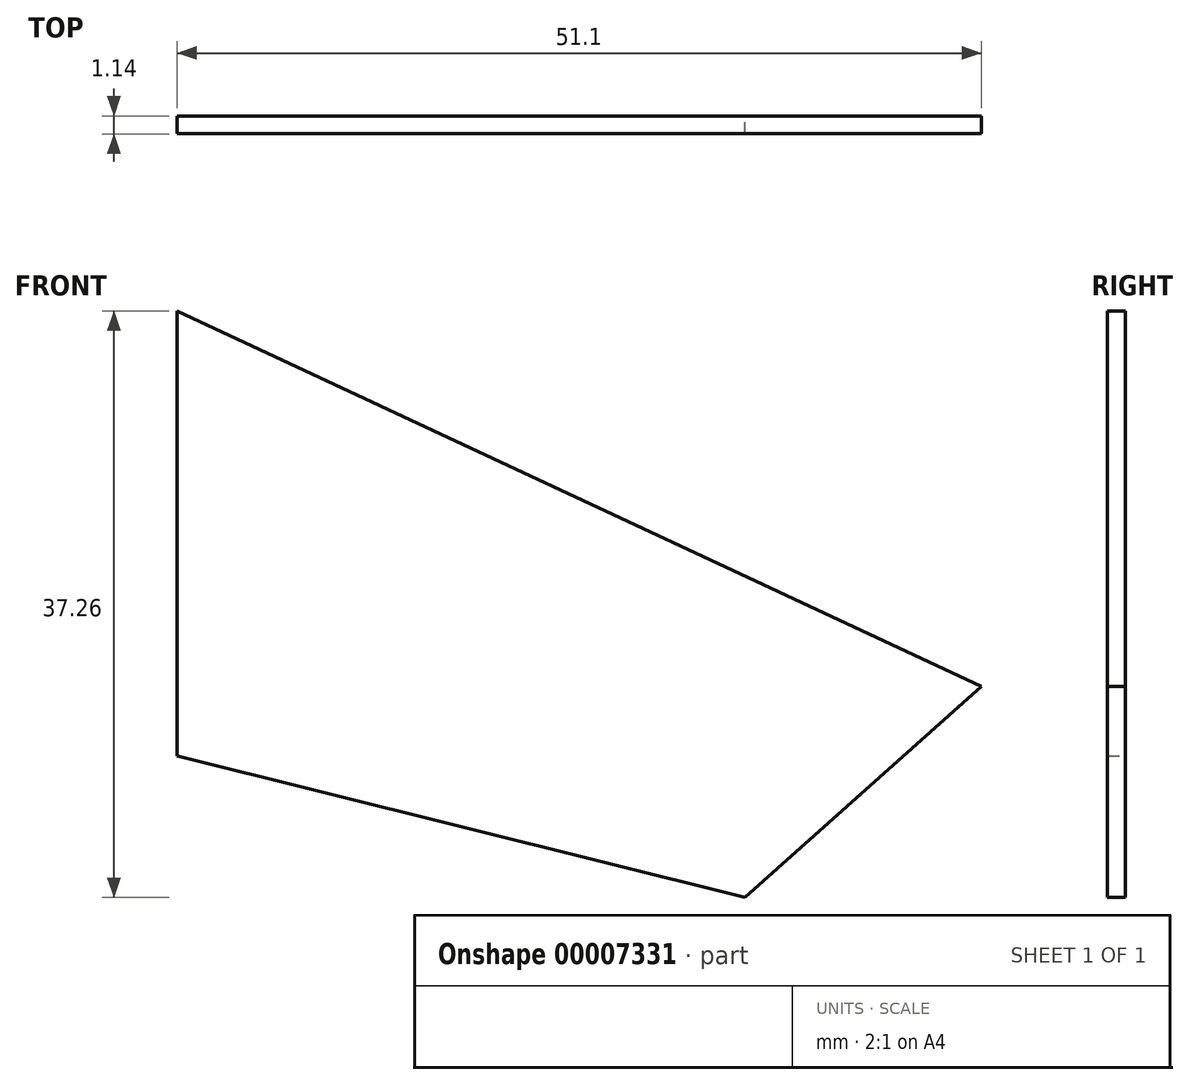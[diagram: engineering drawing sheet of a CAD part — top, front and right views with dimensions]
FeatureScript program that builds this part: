
annotation { "Feature Type Name" : "Feature", "Feature Type Description" : "" }
export const myFeature = defineFeature(function(context is Context, id is Id, definition is map)
    precondition{}
    {
        {
            var Q0;
            Q0=qCreatedBy(makeId("Front.planeOp"),FACE);
            var sketch = newSketch(context, id + "F0", { "sketchPlane" : qUnion([Q0])});
            skLineSegment(sketch, "E0", {"start": v(0, 0) * mm, "end": v(0, 28.27) * mm});
            skLineSegment(sketch, "E1", {"start": v(0, 28.27) * mm, "end": v(51.1, 4.42) * mm});
            skLineSegment(sketch, "E2", {"start": v(51.1, 4.42) * mm, "end": v(36.07, -9) * mm});
            skLineSegment(sketch, "E3", {"start": v(36.07, -9) * mm, "end": v(0, 0) * mm});
            skSolve(sketch);
        }
        {
            var Q0;
            Q0 = qSketchRegion(id + "F0", true);
            extrude(context, id + "F1", {"entities" : qUnion([Q0]), "flatOperationType" : FlatOperationType.REMOVE, "depth" : 0.57 * mm, "offsetDistance" : 25.4 * mm, "domain" : OperationDomain.MODEL});
        }
        {
            var Q0;
            Q0 = qSketchRegion(id + "F0", true);
            extrude(context, id + "F2", {"entities" : qUnion([Q0]), "operationType" : NewBodyOperationType.ADD, "flatOperationType" : FlatOperationType.REMOVE, "oppositeDirection" : true, "depth" : 0.57 * mm, "offsetDistance" : 25.4 * mm, "domain" : OperationDomain.MODEL});
        }
    });
